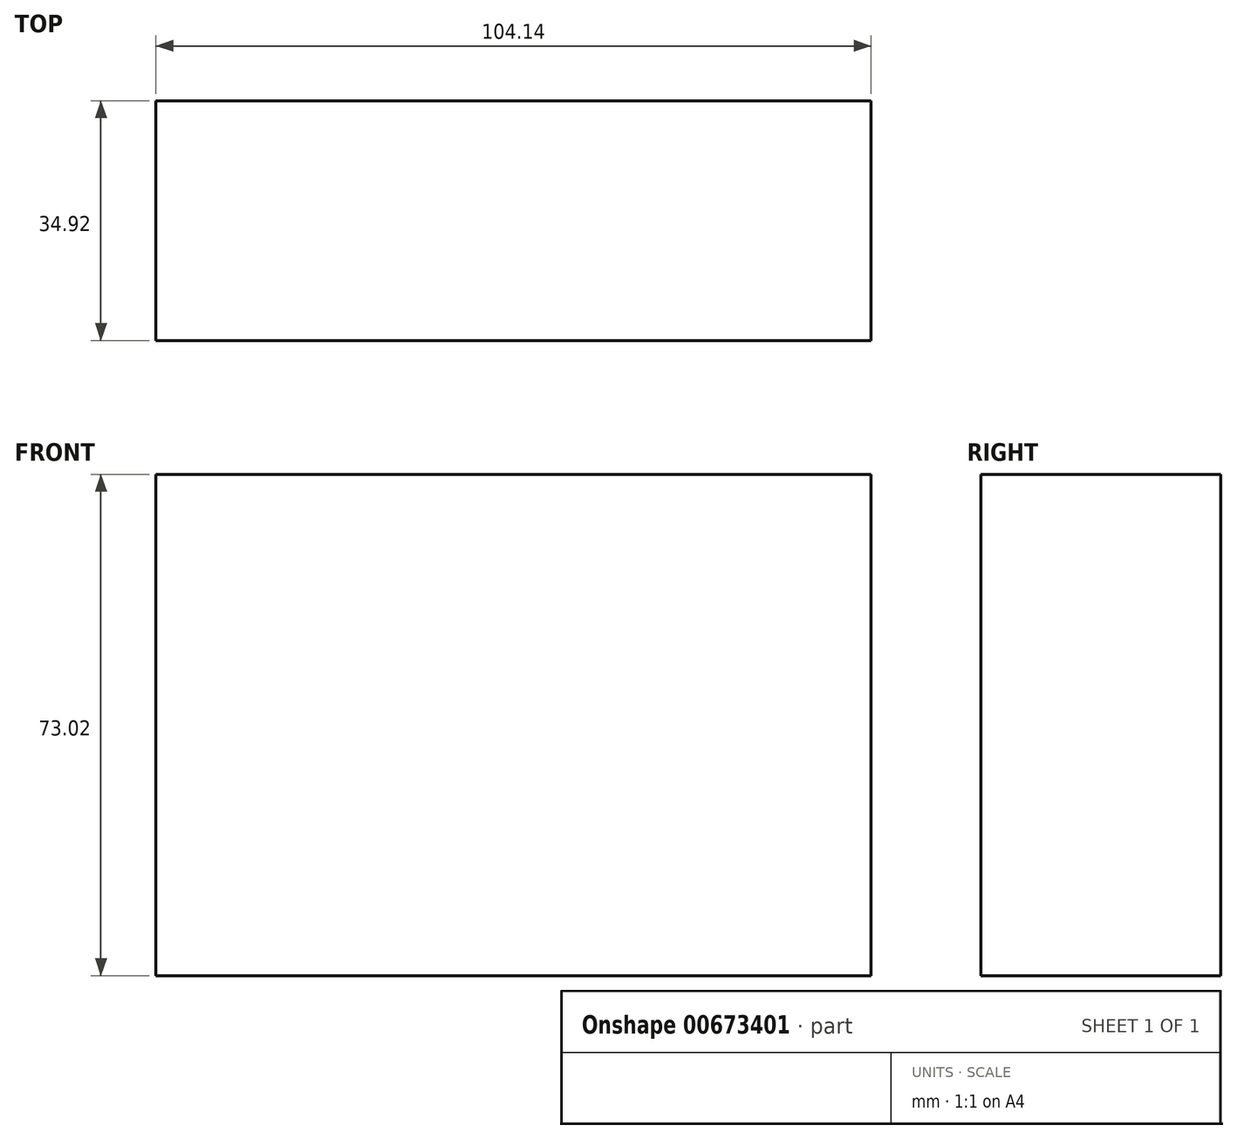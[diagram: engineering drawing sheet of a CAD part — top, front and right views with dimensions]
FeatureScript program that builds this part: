
annotation { "Feature Type Name" : "Feature", "Feature Type Description" : "" }
export const myFeature = defineFeature(function(context is Context, id is Id, definition is map)
    precondition{}
    {
        {
            var Q0;
            Q0=qCreatedBy(makeId("Front.planeOp"),FACE);
            var sketch = newSketch(context, id + "F0", { "sketchPlane" : qUnion([Q0])});
            skLineSegment(sketch, "E0.bottom", {"start": v(52.07, 36.51) * mm, "end": v(-52.07, 36.51) * mm});
            skLineSegment(sketch, "E0.top", {"start": v(52.07, -36.51) * mm, "end": v(-52.07, -36.51) * mm});
            skLineSegment(sketch, "E0.left", {"start": v(52.07, 36.51) * mm, "end": v(52.07, -36.51) * mm});
            skLineSegment(sketch, "E0.right", {"start": v(-52.07, 36.51) * mm, "end": v(-52.07, -36.51) * mm});
            skPoint(sketch, "E0.middle", {"position": v(0, 0) * mm});
            skSolve(sketch);
        }
        {
            var Q0;
            Q0=makeQuery(id+"F0.imprint","IMPRINT",FACE,{"disambiguationData":[TD([[makeQuery(id+"F0.imprint","IMPRINT",EDGE,{"derivedFrom":sQuery(id+"F0.wireOp",EDGE,"E0.bottom")}),1.0]])]});
            extrude(context, id + "F1", {"entities" : qUnion([Q0]), "depth" : 34.92 * mm, "offsetDistance" : 25.4 * mm});
        }
    });
